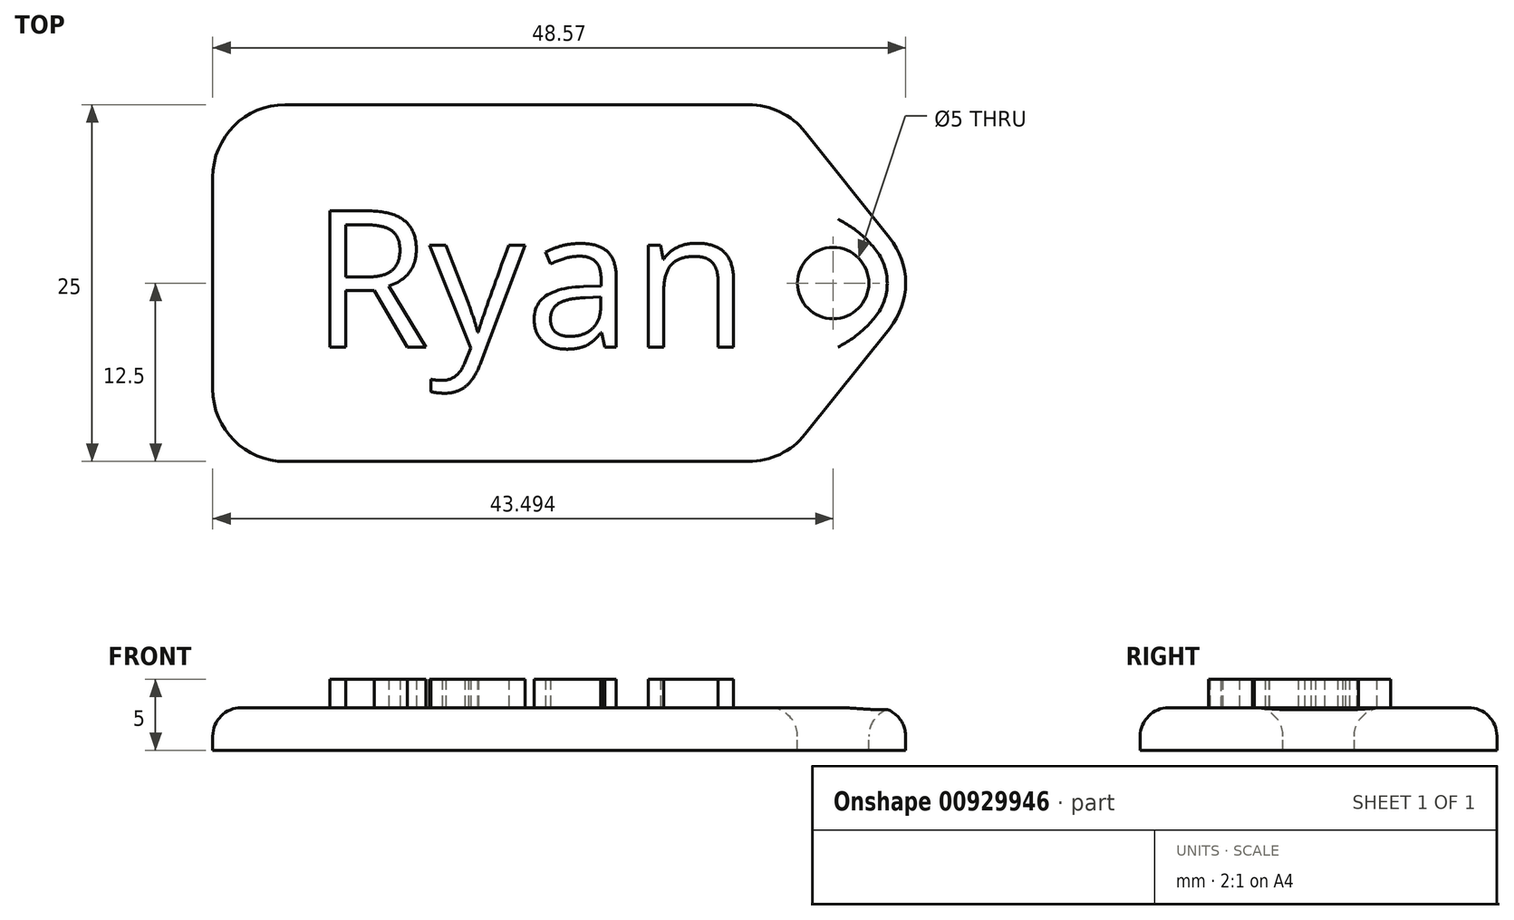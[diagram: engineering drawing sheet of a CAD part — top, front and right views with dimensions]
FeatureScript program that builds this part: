
annotation { "Feature Type Name" : "Feature", "Feature Type Description" : "" }
export const myFeature = defineFeature(function(context is Context, id is Id, definition is map)
    precondition{}
    {
        {
            var Q0;
            Q0=qCreatedBy(makeId("Top.planeOp"),FACE);
            var sketch = newSketch(context, id + "F0", { "sketchPlane" : qUnion([Q0])});
            skLineSegment(sketch, "E0.bottom", {"start": v(20, -12.5) * mm, "end": v(-20, -12.5) * mm});
            skLineSegment(sketch, "E0.top", {"start": v(20, 12.5) * mm, "end": v(-20, 12.5) * mm});
            skLineSegment(sketch, "E0.right", {"start": v(-20, -12.5) * mm, "end": v(-20, 12.5) * mm});
            skPoint(sketch, "E0.middle", {"position": v(0, 0) * mm});
            skPoint(sketch, "E1", {"position": v(30, 0) * mm});
            skLineSegment(sketch, "E2", {"start": v(20, 12.5) * mm, "end": v(30, 0) * mm});
            skLineSegment(sketch, "E3", {"start": v(20, -12.5) * mm, "end": v(30, 0) * mm});
            skSolve(sketch);
        }
        {
            var Q0;
            Q0=makeQuery(id+"F0.imprint","IMPRINT",FACE,{"disambiguationData":[TD([[makeQuery(id+"F0.imprint","IMPRINT",EDGE,{"derivedFrom":sQuery(id+"F0.wireOp",EDGE,"E0.bottom")}),-1.0]])]});
            extrude(context, id + "F1", {"entities" : qUnion([Q0]), "depth" : 3 * mm, "offsetDistance" : 25.4 * mm});
        }
        {
            var Q0;
            Q0=makeQuery(id+"F1.opExtrude","SWEPT_EDGE",EDGE,{"disambiguationData":[OSD([sQuery(id+"F0.wireOp",EDGE,"E0.bottom"),sQuery(id+"F0.wireOp",EDGE,"E3")])]});
            var Q1;
            Q1=makeQuery(id+"F1.opExtrude","SWEPT_EDGE",EDGE,{"disambiguationData":[OSD([sQuery(id+"F0.wireOp",EDGE,"E2"),sQuery(id+"F0.wireOp",EDGE,"E3")])]});
            var Q2;
            Q2=makeQuery(id+"F1.opExtrude","SWEPT_EDGE",EDGE,{"disambiguationData":[OSD([sQuery(id+"F0.wireOp",EDGE,"E0.top"),sQuery(id+"F0.wireOp",EDGE,"E2")])]});
            fillet(context, id + "F2", {"entities" : qUnion([Q0, Q1, Q2]), "radius" : 5.08 * mm, "tangentPropagation" : true, "allowEdgeOverflow" : false});
        }
        {
            var Q0;
            Q0=makeQuery(id+"F1.opExtrude","CAP_FACE",FACE,{"disambiguationData":[OSD([sQuery(id+"F0.wireOp",EDGE,"E0.bottom"),sQuery(id+"F0.wireOp",EDGE,"E0.top"),sQuery(id+"F0.wireOp",EDGE,"E0.right"),sQuery(id+"F0.wireOp",EDGE,"E2"),sQuery(id+"F0.wireOp",EDGE,"E3")])],"isStart":false});
            var sketch = newSketch(context, id + "F3", { "sketchPlane" : qUnion([Q0])});
            skPoint(sketch, "E4", {"position": v(0, 0) * mm});
            skPoint(sketch, "E5", {"position": v(23.5, 0) * mm});
            skSolve(sketch);
        }
        {
            var Q0;
            Q0=sQuery(id+"F3.wireOp",VERTEX,"E5");
            var Q1;
            Q1=makeQuery(id+"F1.opExtrude","SWEPT_BODY",BODY,{"disambiguationData":[OSD([sQuery(id+"F0.wireOp",EDGE,"E0.bottom"),sQuery(id+"F0.wireOp",EDGE,"E0.top"),sQuery(id+"F0.wireOp",EDGE,"E0.right"),sQuery(id+"F0.wireOp",EDGE,"E2"),sQuery(id+"F0.wireOp",EDGE,"E3")])]});
            hole(context, id + "F4", {"style" : HoleStyle.SIMPLE, "endStyle" : HoleEndStyle.THROUGH, "holeDiameter" : 5 * mm, "majorDiameter" : 6.35 * mm, "isTappedThrough" : true, "tappedDepth" : 12.7 * mm, "tapClearance" : 3, "locations" : qUnion([Q0]), "scope" : qUnion([Q1])});
        }
        {
            var Q0;
            Q0=makeQuery(id+"F1.opExtrude","SWEPT_EDGE",EDGE,{"disambiguationData":[OSD([sQuery(id+"F0.wireOp",EDGE,"E0.top"),sQuery(id+"F0.wireOp",EDGE,"E0.right")])]});
            var Q1;
            Q1=makeQuery(id+"F1.opExtrude","SWEPT_EDGE",EDGE,{"disambiguationData":[OSD([sQuery(id+"F0.wireOp",EDGE,"E0.bottom"),sQuery(id+"F0.wireOp",EDGE,"E0.right")])]});
            fillet(context, id + "F5", {"entities" : qUnion([Q0, Q1]), "radius" : 5.08 * mm, "tangentPropagation" : true, "allowEdgeOverflow" : false});
        }
        {
            var Q0;
            Q0=makeQuery(id+"F1.opExtrude","CAP_FACE",FACE,{"disambiguationData":[OSD([sQuery(id+"F0.wireOp",EDGE,"E0.bottom"),sQuery(id+"F0.wireOp",EDGE,"E0.top"),sQuery(id+"F0.wireOp",EDGE,"E0.right"),sQuery(id+"F0.wireOp",EDGE,"E2"),sQuery(id+"F0.wireOp",EDGE,"E3")])],"isStart":false});
            var Q1;
            Q1=makeQuery(id+"F4.hole-0.boolean.opBoolean","COPY",EDGE,{"derivedFrom":makeQuery(id+"F4.hole-0.opRevolve","SWEPT_EDGE",EDGE,{"disambiguationData":[OSD([sQuery(id+"F4.hole-0.sketch.wireOp",EDGE,"core_line_2"),sQuery(id+"F4.hole-0.sketch.wireOp",EDGE,"core_line_3")])]})});
            fillet(context, id + "F6", {"entities" : qUnion([Q0, Q1]), "radius" : 2 * mm, "tangentPropagation" : true, "allowEdgeOverflow" : false});
        }
        {
            var Q0;
            Q0=makeQuery(id+"F1.opExtrude","CAP_FACE",FACE,{"disambiguationData":[OSD([sQuery(id+"F0.wireOp",EDGE,"E0.bottom"),sQuery(id+"F0.wireOp",EDGE,"E0.top"),sQuery(id+"F0.wireOp",EDGE,"E0.right"),sQuery(id+"F0.wireOp",EDGE,"E2"),sQuery(id+"F0.wireOp",EDGE,"E3")])],"isStart":false});
            var sketch = newSketch(context, id + "F7", { "sketchPlane" : qUnion([Q0])});
            skText(sketch, "E6", { "text": "Ryan", "fontName": "OpenSans-Regular.ttf"});
            const initialGuessF7  = {"E6": [-0.0131, -0.0045, 1, 0, 0.00964]};
            skSetInitialGuess(sketch, initialGuessF7);
            skSolve(sketch);
        }
        {
            var Q0;
            Q0 = qSketchRegion(id + "F7", true);
            extrude(context, id + "F8", {"entities" : qUnion([Q0]), "operationType" : NewBodyOperationType.ADD, "depth" : 2 * mm, "offsetDistance" : 25.4 * mm});
        }
    });
